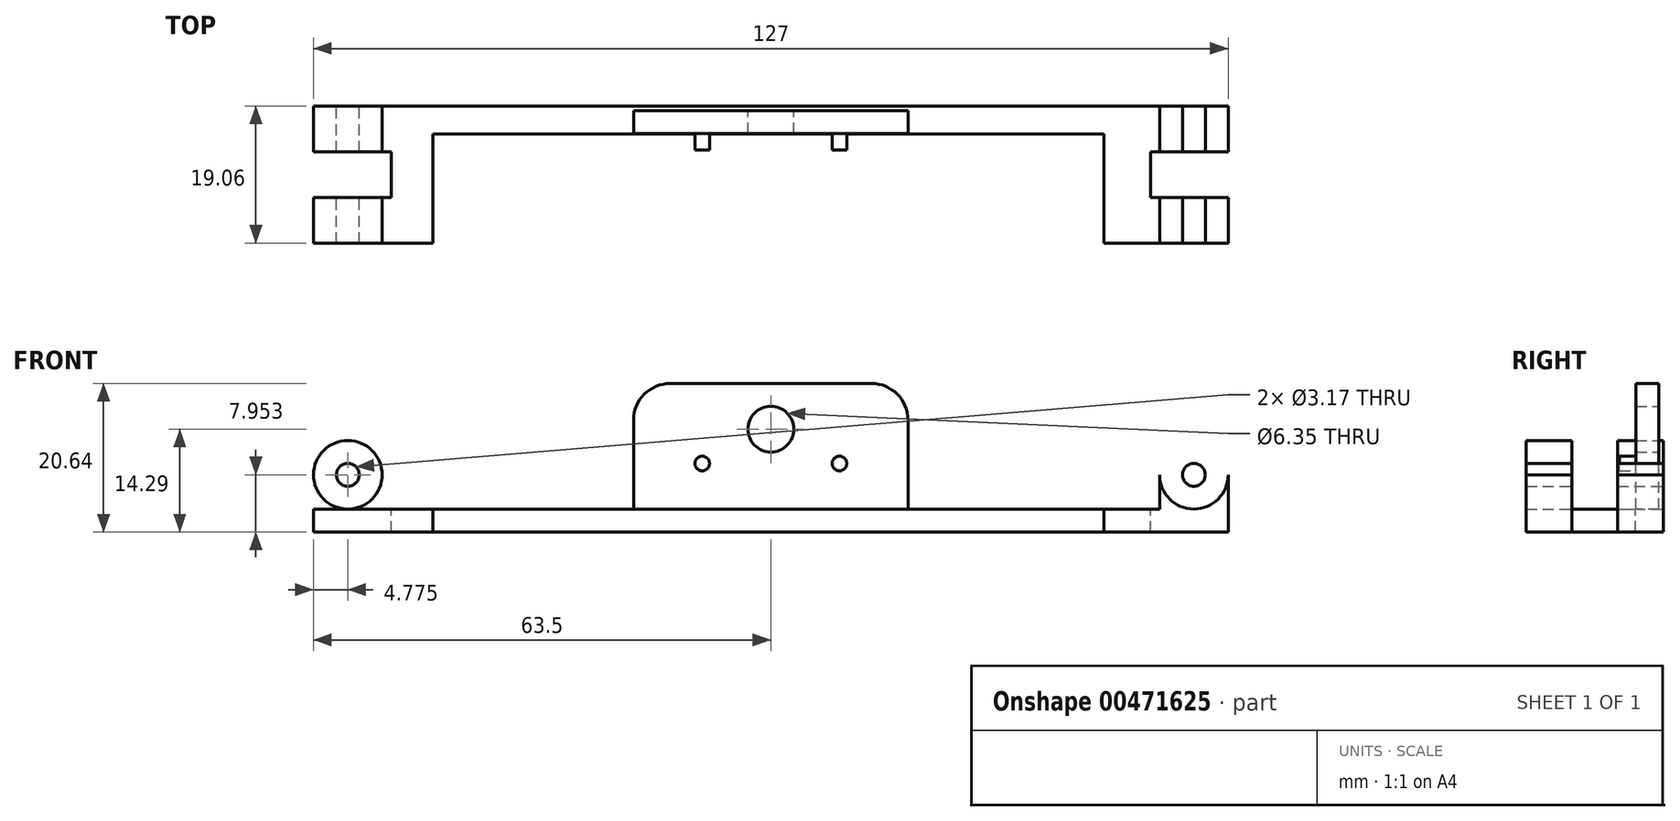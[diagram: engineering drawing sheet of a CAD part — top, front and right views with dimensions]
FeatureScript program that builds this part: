
annotation { "Feature Type Name" : "Feature", "Feature Type Description" : "" }
export const myFeature = defineFeature(function(context is Context, id is Id, definition is map)
    precondition{}
    {
        {
            var Q0;
            Q0=qCreatedBy(makeId("Front.planeOp"),FACE);
            var sketch = newSketch(context, id + "F0", { "sketchPlane" : qUnion([Q0])});
            skLineSegment(sketch, "E0.bottom", {"start": v(-64.04, 61.1) * mm, "end": v(64.52, 61.1) * mm});
            skLineSegment(sketch, "E0.top", {"start": v(-64.04, -64.04) * mm, "end": v(64.52, -64.04) * mm});
            skLineSegment(sketch, "E0.left", {"start": v(-64.04, 61.1) * mm, "end": v(-64.04, -64.04) * mm});
            skLineSegment(sketch, "E0.right", {"start": v(64.52, 61.1) * mm, "end": v(64.52, -64.04) * mm});
            skSolve(sketch);
        }
        {
            var Q0;
            Q0=makeQuery(id+"F0.imprint","IMPRINT",FACE,{"disambiguationData":[TD([[makeQuery(id+"F0.imprint","IMPRINT",EDGE,{"derivedFrom":sQuery(id+"F0.wireOp",EDGE,"E0.bottom")}),-1.0]])]});
            cPlane(context, id + "F1", {"entities" : qUnion([Q0]), "cplaneType" : CPlaneType.OFFSET, "offset" : 8.9 * mm, "oppositeDirection" : true, "width" : 152.4 * mm, "height" : 152.4 * mm});
        }
        {
            var Q0;
            Q0=qCreatedBy(makeId("Front.planeOp"),FACE);
            var sketch = newSketch(context, id + "F2", { "sketchPlane" : qUnion([Q0])});
            skLineSegment(sketch, "E1.bottom", {"start": v(-63.5, -1.59) * mm, "end": v(63.5, -1.59) * mm});
            skLineSegment(sketch, "E1.top", {"start": v(-63.5, 1.59) * mm, "end": v(63.5, 1.59) * mm});
            skLineSegment(sketch, "E1.left", {"start": v(-63.5, -1.59) * mm, "end": v(-63.5, 1.59) * mm});
            skLineSegment(sketch, "E1.right", {"start": v(63.5, -1.59) * mm, "end": v(63.5, 1.59) * mm});
            skPoint(sketch, "E1.middle", {"position": v(0, 0) * mm});
            skCircle(sketch, "E2", {"center": v(-58.72, 6.36) * mm, "radius": 1.59 * mm});
            skLineSegment(sketch, "E3", {"start": v(0, 46.13) * mm, "end": v(0, -43.3) * mm, "construction": true});
            skCircle(sketch, "E4.0", {"center": v(-58.72, 6.36) * mm, "radius": 4.76 * mm});
            skLineSegment(sketch, "E5.bottom", {"start": v(-63.5, 1.59) * mm, "end": v(-53.96, 1.59) * mm});
            skLineSegment(sketch, "E5.top", {"start": v(-63.5, 6.36) * mm, "end": v(-63.49, 6.36) * mm});
            skLineSegment(sketch, "E5.left", {"start": v(-63.5, 1.59) * mm, "end": v(-63.5, 6.36) * mm});
            skLineSegment(sketch, "E5.right", {"start": v(-53.96, 1.59) * mm, "end": v(-53.96, 6.36) * mm});
            skCircle(sketch, "E6.MirrorC", {"center": v(58.72, 6.36) * mm, "radius": 4.76 * mm});
            skCircle(sketch, "E7.MirrorC", {"center": v(58.72, 6.36) * mm, "radius": 1.59 * mm});
            skLineSegment(sketch, "E8.MirrorCS", {"start": v(53.96, 1.59) * mm, "end": v(53.96, 6.36) * mm});
            skLineSegment(sketch, "E9.MirrorCS", {"start": v(63.5, 1.59) * mm, "end": v(63.5, 6.36) * mm});
            skLineSegment(sketch, "E10.trimOffspring", {"start": v(63.49, 6.36) * mm, "end": v(63.5, 6.36) * mm});
            skSolve(sketch);
        }
        {
            var Q0;
            Q0=qCreatedBy(makeId("Front.planeOp"),FACE);
            var sketch = newSketch(context, id + "F3", { "sketchPlane" : qUnion([Q0])});
            skLineSegment(sketch, "E11.bottom", {"start": v(-64.66, -4.33) * mm, "end": v(-52.7, -4.33) * mm});
            skLineSegment(sketch, "E11.top", {"start": v(-64.66, 13.02) * mm, "end": v(-52.7, 13.02) * mm});
            skLineSegment(sketch, "E11.left", {"start": v(-64.66, -4.33) * mm, "end": v(-64.66, 13.02) * mm});
            skLineSegment(sketch, "E11.right", {"start": v(-52.7, -4.33) * mm, "end": v(-52.7, 13.02) * mm});
            skLineSegment(sketch, "E12", {"start": v(0, 34.79) * mm, "end": v(0, -36.9) * mm, "construction": true});
            skLineSegment(sketch, "E13.MirrorCS", {"start": v(64.66, -4.33) * mm, "end": v(52.7, -4.33) * mm});
            skLineSegment(sketch, "E14.MirrorCS", {"start": v(52.7, -4.33) * mm, "end": v(52.7, 13.02) * mm});
            skLineSegment(sketch, "E15.MirrorCS", {"start": v(64.66, 13.02) * mm, "end": v(52.7, 13.02) * mm});
            skLineSegment(sketch, "E16.MirrorCS", {"start": v(64.66, -4.33) * mm, "end": v(64.66, 13.02) * mm});
            skSolve(sketch);
        }
        {
            var Q0;
            Q0=makeQuery(id+"F2.imprint","IMPRINT",FACE,{"disambiguationData":[TD([[makeQuery(id+"F2.imprint","IMPRINT",EDGE,{"derivedFrom":sQuery(id+"F2.wireOp",EDGE,"E7.MirrorC")}),1.0]])]});
            var Q1;
            {var subQ1=sQuery(id+"F2.wireOp",EDGE,"E8.MirrorCS");Q1=makeQuery(id+"F2.imprint","IMPRINT",FACE,{"disambiguationData":[TD([[makeQuery(id+"F2.imprint","IMPRINT",EDGE,{"derivedFrom":subQ1}),-1.0]])]});}
            var Q2;
            Q2=makeQuery(id+"F2.imprint","IMPRINT",FACE,{"disambiguationData":[TD([[makeQuery(id+"F2.imprint","IMPRINT",EDGE,{"derivedFrom":sQuery(id+"F2.wireOp",EDGE,"E1.bottom")}),1.0]])]});
            var Q3;
            Q3=makeQuery(id+"F2.imprint","IMPRINT",FACE,{"disambiguationData":[TD([[makeQuery(id+"F2.imprint","IMPRINT",EDGE,{"derivedFrom":sQuery(id+"F2.wireOp",EDGE,"E2")}),-1.0]])]});
            var Q4;
            Q4=makeQuery(id+"F2.imprint","IMPRINT",FACE,{"disambiguationData":[TD([[makeQuery(id+"F2.imprint","IMPRINT",EDGE,{"derivedFrom":sQuery(id+"F2.wireOp",EDGE,"E5.bottom")}),1.0]])]});
            extrude(context, id + "F4", {"entities" : qUnion([Q0, Q1, Q2, Q3, Q4]), "depth" : 19.05 * mm, "symmetric" : true});
        }
        {
            var Q0;
            Q0 = qSketchRegion(id + "F3", true);
            extrude(context, id + "F5", {"entities" : qUnion([Q0]), "operationType" : NewBodyOperationType.REMOVE, "oppositeDirection" : true, "depth" : 6.35 * mm, "symmetric" : true});
        }
        {
            var Q0;
            Q0=qCreatedBy(id+"F1.planeOp",FACE);
            var sketch = newSketch(context, id + "F6", { "sketchPlane" : qUnion([Q0])});
            skLineSegment(sketch, "E17.top", {"start": v(19.05, 19.05) * mm, "end": v(-19.05, 19.05) * mm});
            skLineSegment(sketch, "E17.left", {"start": v(19.05, 0) * mm, "end": v(19.05, 19.05) * mm});
            skLineSegment(sketch, "E17.right", {"start": v(-19.05, 0) * mm, "end": v(-19.05, 19.05) * mm});
            skPoint(sketch, "E17.middle", {"position": v(0, 0) * mm});
            skPoint(sketch, "E18", {"position": v(-19.05, 0) * mm});
            skPoint(sketch, "E19", {"position": v(19.05, 0) * mm});
            skLineSegment(sketch, "E20", {"start": v(-19.05, 0) * mm, "end": v(19.05, 0) * mm});
            skSolve(sketch);
        }
        {
            var Q0;
            Q0=makeQuery(id+"F6.imprint","IMPRINT",FACE,{"disambiguationData":[TD([[makeQuery(id+"F6.imprint","IMPRINT",EDGE,{"derivedFrom":sQuery(id+"F6.wireOp",EDGE,"E17.top")}),1.0]])]});
            extrude(context, id + "F7", {"entities" : qUnion([Q0]), "operationType" : NewBodyOperationType.ADD, "depth" : 3.17 * mm});
        }
        {
            var Q0;
            Q0=qCreatedBy(id+"F1.planeOp",FACE);
            var sketch = newSketch(context, id + "F8", { "sketchPlane" : qUnion([Q0])});
            skCircle(sketch, "E21", {"center": v(-9.53, 7.94) * mm, "radius": 1.02 * mm});
            skCircle(sketch, "E22", {"center": v(9.52, 7.94) * mm, "radius": 1.02 * mm});
            skSolve(sketch);
        }
        {
            var Q0;
            Q0 = qSketchRegion(id + "F8", true);
            extrude(context, id + "F9", {"entities" : qUnion([Q0]), "operationType" : NewBodyOperationType.ADD, "depth" : 5.47 * mm});
        }
        {
            var Q0;
            Q0=makeQuery(id+"F7.opExtrude","SWEPT_EDGE",EDGE,{"disambiguationData":[OSD([sQuery(id+"F6.wireOp",EDGE,"E17.top"),sQuery(id+"F6.wireOp",EDGE,"E17.left")])]});
            var Q1;
            Q1=makeQuery(id+"F7.opExtrude","SWEPT_EDGE",EDGE,{"disambiguationData":[OSD([sQuery(id+"F6.wireOp",EDGE,"E17.top"),sQuery(id+"F6.wireOp",EDGE,"E17.right")])]});
            fillet(context, id + "F10", {"entities" : qUnion([Q0, Q1]), "radius" : 5.08 * mm, "tangentPropagation" : true, "allowEdgeOverflow" : false});
        }
        {
            var Q0;
            Q0=qCreatedBy(makeId("Top.planeOp"),FACE);
            var sketch = newSketch(context, id + "F11", { "sketchPlane" : qUnion([Q0])});
            skLineSegment(sketch, "E23.bottom", {"start": v(46.26, -13.23) * mm, "end": v(-46.93, -13.23) * mm});
            skLineSegment(sketch, "E23.top", {"start": v(46.26, 5.64) * mm, "end": v(-46.93, 5.64) * mm});
            skLineSegment(sketch, "E23.left", {"start": v(46.26, -13.23) * mm, "end": v(46.26, 5.64) * mm});
            skLineSegment(sketch, "E23.right", {"start": v(-46.93, -13.23) * mm, "end": v(-46.93, 5.64) * mm});
            skSolve(sketch);
        }
        {
            var Q0;
            Q0=makeQuery(id+"F11.imprint","IMPRINT",FACE,{"disambiguationData":[TD([[makeQuery(id+"F11.imprint","IMPRINT",EDGE,{"derivedFrom":sQuery(id+"F11.wireOp",EDGE,"E23.bottom")}),-1.0]])]});
            extrude(context, id + "F12", {"entities" : qUnion([Q0]), "operationType" : NewBodyOperationType.REMOVE, "oppositeDirection" : true, "depth" : 6.35 * mm, "symmetric" : true});
        }
        {
            var Q0;
            Q0=qCreatedBy(id+"F1.planeOp",FACE);
            var sketch = newSketch(context, id + "F13", { "sketchPlane" : qUnion([Q0])});
            skCircle(sketch, "E24", {"center": v(0, 12.7) * mm, "radius": 3.18 * mm});
            skSolve(sketch);
        }
        {
            var Q0;
            Q0 = qSketchRegion(id + "F13", true);
            extrude(context, id + "F14", {"entities" : qUnion([Q0]), "operationType" : NewBodyOperationType.REMOVE, "depth" : 9.5 * mm});
        }
    });
